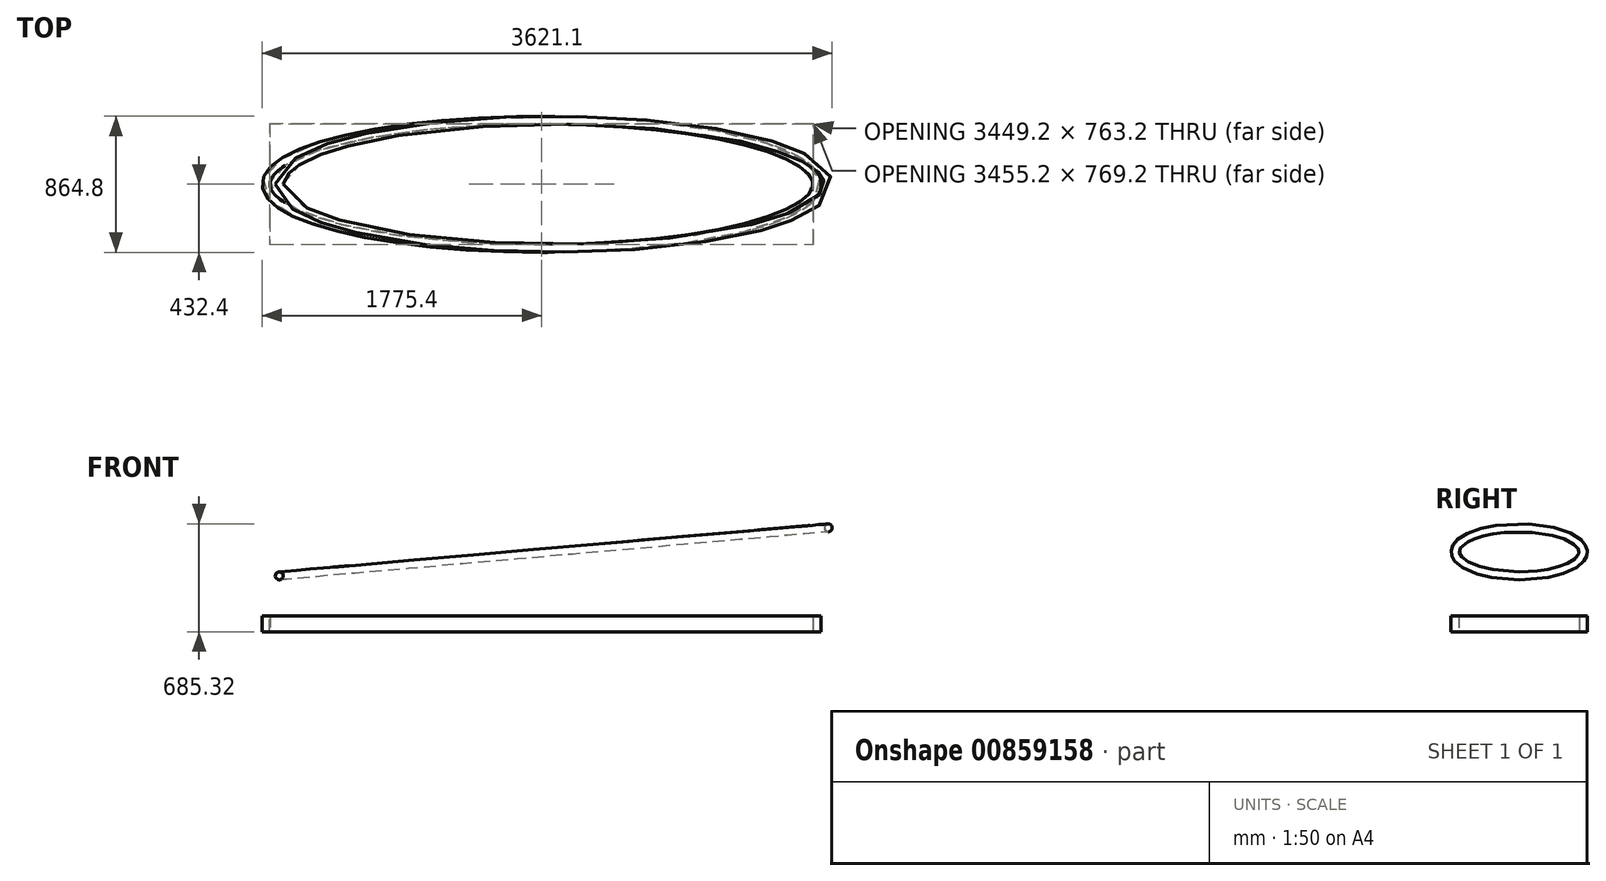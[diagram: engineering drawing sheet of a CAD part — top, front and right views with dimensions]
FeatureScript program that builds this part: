
annotation { "Feature Type Name" : "Feature", "Feature Type Description" : "" }
export const myFeature = defineFeature(function(context is Context, id is Id, definition is map)
    precondition{}
    {
        {
            var Q0;
            Q0=qCreatedBy(makeId("Top.planeOp"),FACE);
            var sketch = newSketch(context, id + "F0", { "sketchPlane" : qUnion([Q0])});
            skLineSegment(sketch, "E0.bottom", {"start": v(-1500, 407) * mm, "end": v(1500, 407) * mm, "construction": true});
            skLineSegment(sketch, "E0.top", {"start": v(-1500, -407) * mm, "end": v(1500, -407) * mm, "construction": true});
            skLineSegment(sketch, "E0.left", {"start": v(-1500, 407) * mm, "end": v(-1500, -407) * mm, "construction": true});
            skLineSegment(sketch, "E0.right", {"start": v(1500, 407) * mm, "end": v(1500, -407) * mm, "construction": true});
            skLineSegment(sketch, "E1", {"start": v(0, 407) * mm, "end": v(0, -407) * mm});
            skLineSegment(sketch, "E2.bottom", {"start": v(1080, 117.5) * mm, "end": v(1750, 117.5) * mm, "construction": true});
            skLineSegment(sketch, "E2.top", {"start": v(1080, -117.5) * mm, "end": v(1750, -117.5) * mm, "construction": true});
            skLineSegment(sketch, "E2.left", {"start": v(1080, 117.5) * mm, "end": v(1080, -117.5) * mm, "construction": true});
            skLineSegment(sketch, "E2.right", {"start": v(1750, 117.5) * mm, "end": v(1750, -117.5) * mm, "construction": true});
            skLineSegment(sketch, "E3.bottom", {"start": v(-1500, 677.5) * mm, "end": v(-801, 677.5) * mm, "construction": true});
            skLineSegment(sketch, "E3.top", {"start": v(-1500, 522.5) * mm, "end": v(-801, 522.5) * mm, "construction": true});
            skLineSegment(sketch, "E3.left", {"start": v(-1500, 677.5) * mm, "end": v(-1500, 522.5) * mm, "construction": true});
            skLineSegment(sketch, "E3.right", {"start": v(-801, 677.5) * mm, "end": v(-801, 522.5) * mm, "construction": true});
            skEllipse(sketch, "E4", {"center": v(0, 0) * mm, "majorRadius": 407 * mm, "minorRadius": 1750 * mm, "majorAxis": v(0, 1)});
            skLineSegment(sketch, "E5", {"start": v(-1500, 0) * mm, "end": v(1750, 0) * mm, "construction": true});
            skSolve(sketch);
        }
        {
            var Q0;
            Q0=qCreatedBy(makeId("Right.planeOp"),FACE);
            var sketch = newSketch(context, id + "F1", { "sketchPlane" : qUnion([Q0])});
            skLineSegment(sketch, "E6.bottom", {"start": v(-432.4, 50.8) * mm, "end": v(-381.6, 50.8) * mm});
            skLineSegment(sketch, "E6.top", {"start": v(-432.4, -50.8) * mm, "end": v(-381.6, -50.8) * mm});
            skLineSegment(sketch, "E6.left", {"start": v(-432.4, 50.8) * mm, "end": v(-432.4, -50.8) * mm});
            skLineSegment(sketch, "E6.right", {"start": v(-381.6, 50.8) * mm, "end": v(-381.6, -50.8) * mm});
            skLineSegment(sketch, "E7", {"start": v(-381.6, 50.8) * mm, "end": v(-432.4, -50.8) * mm, "construction": true});
            skLineSegment(sketch, "E8", {"start": v(0, 0) * mm, "end": v(-407, 0) * mm, "construction": true});
            skLineSegment(sketch, "E9.0", {"start": v(-429.4, 47.8) * mm, "end": v(-384.6, 47.8) * mm});
            skLineSegment(sketch, "E9.1", {"start": v(-429.4, 47.8) * mm, "end": v(-429.4, -47.8) * mm});
            skLineSegment(sketch, "E9.2", {"start": v(-429.4, -47.8) * mm, "end": v(-384.6, -47.8) * mm});
            skLineSegment(sketch, "E9.3", {"start": v(-384.6, 47.8) * mm, "end": v(-384.6, -47.8) * mm});
            skSolve(sketch);
        }
        {
            var Q0;
            Q0=makeQuery(id+"F1.imprint","IMPRINT",FACE,{"disambiguationData":[TD([[makeQuery(id+"F1.imprint","IMPRINT",EDGE,{"derivedFrom":sQuery(id+"F1.wireOp",EDGE,"E6.bottom")}),-1.0]])]});
            var Q1;
            Q1=sQuery(id+"F0.wireOp",EDGE,"E4");
            sweep(context, id + "F2", {"profiles" : qUnion([Q0]), "path" : qUnion([Q1])});
        }
        {
            var Q0;
            Q0=qCreatedBy(makeId("Front.planeOp"),FACE);
            var sketch = newSketch(context, id + "F3", { "sketchPlane" : qUnion([Q0])});
            skLineSegment(sketch, "E10", {"start": v(0, 0) * mm, "end": v(0, 450) * mm, "construction": true});
            skLineSegment(sketch, "E11", {"start": v(-1992.39, 275.69) * mm, "end": v(0, 450) * mm, "construction": true});
            skSolve(sketch);
        }
        {
            var Q0;
            Q0=sQuery(id+"F3.wireOp",EDGE,"E11");
            cPlane(context, id + "F4", {"entities" : qUnion([Q0]), "cplaneType" : CPlaneType.LINE_ANGLE, "offset" : 25 * mm, "angle" : 90 * degree, "oppositeDirection" : true, "width" : 150 * mm, "height" : 150 * mm});
        }
        {
            var Q0;
            Q0=qCreatedBy(id+"F4.planeOp",FACE);
            var sketch = newSketch(context, id + "F5", { "sketchPlane" : qUnion([Q0])});
            skEllipse(sketch, "E12", {"center": v(116.92, 0) * mm, "majorRadius": 407 * mm, "minorRadius": 1750 * mm, "majorAxis": v(0, 1)});
            skLineSegment(sketch, "E13", {"start": v(-1633.08, 0) * mm, "end": v(1866.92, 0) * mm, "construction": true});
            skSolve(sketch);
        }
        {
            var Q0;
            Q0=sQuery(id+"F3.wireOp",EDGE,"E11");
            cPlane(context, id + "F6", {"entities" : qUnion([Q0]), "cplaneType" : CPlaneType.LINE_ANGLE, "offset" : 25 * mm, "angle" : 0 * degree, "width" : 150 * mm, "height" : 150 * mm});
        }
        {
            var Q0;
            Q0=qCreatedBy(id+"F6.planeOp",FACE);
            var sketch = newSketch(context, id + "F7", { "sketchPlane" : qUnion([Q0])});
            skCircle(sketch, "E14", {"center": v(1665.64, 304.28) * mm, "radius": 25.25 * mm});
            skCircle(sketch, "E15", {"center": v(1665.64, 304.28) * mm, "radius": 22.4 * mm});
            skSolve(sketch);
        }
        {
            var Q0;
            Q0=makeQuery(id+"F7.imprint","IMPRINT",FACE,{"disambiguationData":[TD([[makeQuery(id+"F7.imprint","IMPRINT",EDGE,{"derivedFrom":sQuery(id+"F7.wireOp",EDGE,"E14")}),1.0]])]});
            var Q1;
            Q1=sQuery(id+"F5.wireOp",EDGE,"E12");
            sweep(context, id + "F8", {"profiles" : qUnion([Q0]), "path" : qUnion([Q1])});
        }
    });
